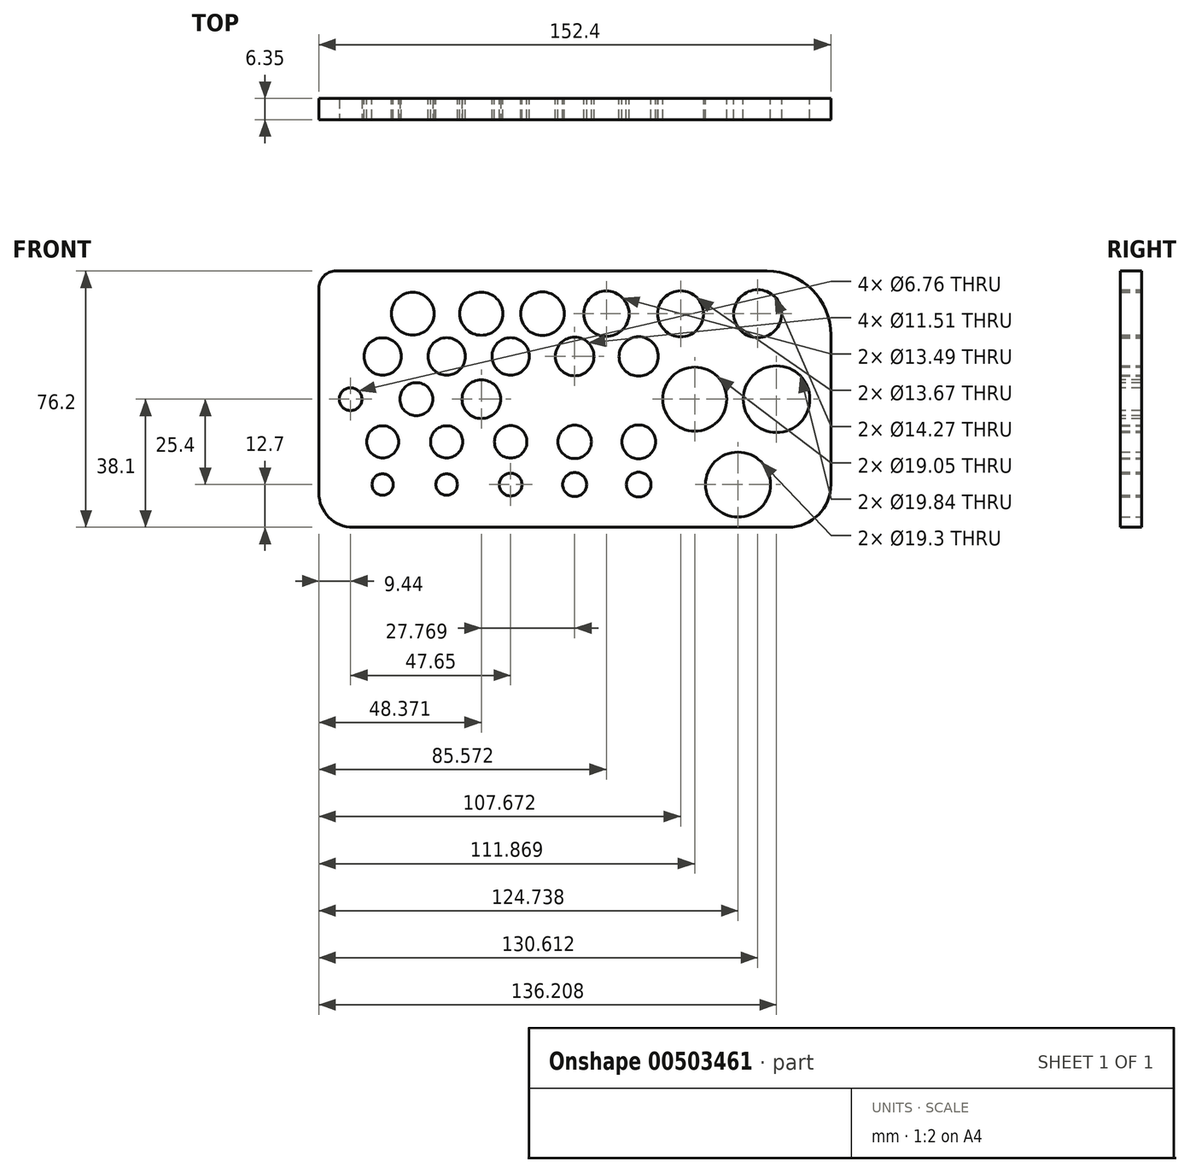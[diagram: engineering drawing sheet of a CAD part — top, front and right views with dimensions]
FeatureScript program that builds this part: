
annotation { "Feature Type Name" : "Feature", "Feature Type Description" : "" }
export const myFeature = defineFeature(function(context is Context, id is Id, definition is map)
    precondition{}
    {
        {
            var Q0;
            Q0=qCreatedBy(makeId("Front.planeOp"),FACE);
            var sketch = newSketch(context, id + "F0", { "sketchPlane" : qUnion([Q0])});
            skLineSegment(sketch, "E0.bottom", {"start": v(-76.2, 38.1) * mm, "end": v(76.2, 38.1) * mm});
            skLineSegment(sketch, "E0.top", {"start": v(-76.2, -38.1) * mm, "end": v(76.2, -38.1) * mm});
            skLineSegment(sketch, "E0.left", {"start": v(-76.2, 38.1) * mm, "end": v(-76.2, -38.1) * mm});
            skLineSegment(sketch, "E0.right", {"start": v(76.2, 38.1) * mm, "end": v(76.2, -38.1) * mm});
            skPoint(sketch, "E0.middle", {"position": v(0, 0) * mm});
            skLineSegment(sketch, "E1", {"start": v(-76.2, 0) * mm, "end": v(76.2, 0) * mm, "construction": true});
            skLineSegment(sketch, "E2", {"start": v(-76.2, 25.4) * mm, "end": v(76.2, 25.4) * mm, "construction": true});
            skLineSegment(sketch, "E3", {"start": v(76.2, -25.4) * mm, "end": v(-76.2, -25.4) * mm, "construction": true});
            skPoint(sketch, "E4", {"position": v(-57.2, -25.4) * mm});
            skCircle(sketch, "E5", {"center": v(-38.16, -25.4) * mm, "radius": 3.2 * mm});
            skCircle(sketch, "E6", {"center": v(-57.2, -25.4) * mm, "radius": 3.18 * mm});
            skCircle(sketch, "E7", {"center": v(-19.1, -25.4) * mm, "radius": 3.38 * mm});
            skCircle(sketch, "E8", {"center": v(-0.06, -25.4) * mm, "radius": 3.57 * mm});
            skCircle(sketch, "E9", {"center": v(19, -25.4) * mm, "radius": 3.68 * mm});
            skLineSegment(sketch, "E10", {"start": v(-76.2, 12.7) * mm, "end": v(76.2, 12.7) * mm, "construction": true});
            skLineSegment(sketch, "E11.MirrorCS", {"start": v(-76.2, -12.7) * mm, "end": v(76.2, -12.7) * mm, "construction": true});
            skPoint(sketch, "E12", {"position": v(-57.2, 12.7) * mm});
            skPoint(sketch, "E13", {"position": v(-57.2, 0) * mm});
            skPoint(sketch, "E14", {"position": v(-57.2, -12.7) * mm});
            skPoint(sketch, "E15", {"position": v(-38.16, 12.7) * mm});
            skPoint(sketch, "E16", {"position": v(-38.16, 0) * mm});
            skPoint(sketch, "E17", {"position": v(-38.16, -12.7) * mm});
            skPoint(sketch, "E18", {"position": v(-19.1, 12.7) * mm});
            skPoint(sketch, "E19", {"position": v(-19.1, 0) * mm});
            skPoint(sketch, "E20", {"position": v(-19.1, -12.7) * mm});
            skPoint(sketch, "E21", {"position": v(-0.06, 12.7) * mm});
            skPoint(sketch, "E22", {"position": v(-0.06, -12.7) * mm});
            skPoint(sketch, "E23", {"position": v(19, 12.7) * mm});
            skPoint(sketch, "E24", {"position": v(19, 0) * mm});
            skPoint(sketch, "E25", {"position": v(19, -12.7) * mm});
            skCircle(sketch, "E26", {"center": v(-57.2, -12.7) * mm, "radius": 4.76 * mm});
            skCircle(sketch, "E27", {"center": v(-38.16, -12.7) * mm, "radius": 4.79 * mm});
            skCircle(sketch, "E28", {"center": v(-19.1, -12.7) * mm, "radius": 4.83 * mm});
            skCircle(sketch, "E29", {"center": v(-0.06, -12.7) * mm, "radius": 4.97 * mm});
            skCircle(sketch, "E30", {"center": v(19, -12.7) * mm, "radius": 5.04 * mm});
            skCircle(sketch, "E31", {"center": v(-57.2, 12.7) * mm, "radius": 5.56 * mm});
            skCircle(sketch, "E32", {"center": v(-38.16, 12.7) * mm, "radius": 5.56 * mm});
            skCircle(sketch, "E33", {"center": v(-19.1, 12.7) * mm, "radius": 5.57 * mm});
            skCircle(sketch, "E34", {"center": v(-0.06, 12.7) * mm, "radius": 5.75 * mm});
            skCircle(sketch, "E35", {"center": v(19, 12.7) * mm, "radius": 5.84 * mm});
            skPoint(sketch, "E36", {"position": v(-48.26, 25.4) * mm});
            skPoint(sketch, "E37", {"position": v(-27.84, 25.4) * mm});
            skPoint(sketch, "E38", {"position": v(-9.65, 25.4) * mm});
            skPoint(sketch, "E39", {"position": v(9.37, 25.4) * mm});
            skCircle(sketch, "E40", {"center": v(-48.26, 25.4) * mm, "radius": 6.35 * mm});
            skCircle(sketch, "E41", {"center": v(-27.84, 25.4) * mm, "radius": 6.41 * mm});
            skCircle(sketch, "E42", {"center": v(-9.65, 25.4) * mm, "radius": 6.48 * mm});
            skCircle(sketch, "E43", {"center": v(9.37, 25.4) * mm, "radius": 6.74 * mm});
            skPoint(sketch, "E44", {"position": v(31.47, 25.4) * mm});
            skCircle(sketch, "E45", {"center": v(31.47, 25.4) * mm, "radius": 6.83 * mm});
            skPoint(sketch, "E46", {"position": v(54.41, 25.4) * mm});
            skCircle(sketch, "E47", {"center": v(54.41, 25.4) * mm, "radius": 7.14 * mm});
            skPoint(sketch, "E48", {"position": v(34.55, -12.7) * mm});
            skCircle(sketch, "E49", {"center": v(35.67, 0) * mm, "radius": 9.53 * mm});
            skCircle(sketch, "E50", {"center": v(60, 0) * mm, "radius": 9.92 * mm});
            skCircle(sketch, "E51", {"center": v(48.54, -25.4) * mm, "radius": 9.65 * mm});
            skSolve(sketch);
        }
        {
            var Q0;
            Q0=makeQuery(id+"F0.imprint","IMPRINT",FACE,{"disambiguationData":[TD([[makeQuery(id+"F0.imprint","IMPRINT",EDGE,{"derivedFrom":sQuery(id+"F0.wireOp",EDGE,"E0.bottom")}),-1.0]])]});
            extrude(context, id + "F1", {"entities" : qUnion([Q0]), "depth" : 6.35 * mm, "offsetDistance" : 25.4 * mm});
        }
        {
            var Q0;
            Q0=makeQuery(id+"F1.opExtrude","SWEPT_EDGE",EDGE,{"disambiguationData":[OSD([sQuery(id+"F0.wireOp",EDGE,"E0.bottom"),sQuery(id+"F0.wireOp",EDGE,"E0.left")])]});
            fillet(context, id + "F2", {"entities" : qUnion([Q0]), "radius" : 5.08 * mm, "tangentPropagation" : true, "allowEdgeOverflow" : false});
        }
        {
            var Q0;
            Q0=makeQuery(id+"F1.opExtrude","SWEPT_EDGE",EDGE,{"disambiguationData":[OSD([sQuery(id+"F0.wireOp",EDGE,"E0.top"),sQuery(id+"F0.wireOp",EDGE,"E0.left")])]});
            fillet(context, id + "F3", {"entities" : qUnion([Q0]), "radius" : 10.16 * mm, "tangentPropagation" : true, "allowEdgeOverflow" : false});
        }
        {
            var Q0;
            Q0=makeQuery(id+"F1.opExtrude","SWEPT_EDGE",EDGE,{"disambiguationData":[OSD([sQuery(id+"F0.wireOp",EDGE,"E0.top"),sQuery(id+"F0.wireOp",EDGE,"E0.right")])]});
            fillet(context, id + "F4", {"entities" : qUnion([Q0]), "radius" : 12.7 * mm, "tangentPropagation" : true, "allowEdgeOverflow" : false});
        }
        {
            var Q0;
            Q0=makeQuery(id+"F1.opExtrude","SWEPT_EDGE",EDGE,{"disambiguationData":[OSD([sQuery(id+"F0.wireOp",EDGE,"E0.bottom"),sQuery(id+"F0.wireOp",EDGE,"E0.right")])]});
            fillet(context, id + "F5", {"entities" : qUnion([Q0]), "radius" : 19.05 * mm, "tangentPropagation" : true, "allowEdgeOverflow" : false});
        }
        {
            var Q0;
            Q0=makeQuery(id+"F1.opExtrude","CAP_FACE",FACE,{"disambiguationData":[OSD([sQuery(id+"F0.wireOp",EDGE,"E0.bottom"),sQuery(id+"F0.wireOp",EDGE,"E0.top"),sQuery(id+"F0.wireOp",EDGE,"E0.left"),sQuery(id+"F0.wireOp",EDGE,"E0.right"),sQuery(id+"F0.wireOp",EDGE,"E5"),sQuery(id+"F0.wireOp",EDGE,"E6"),sQuery(id+"F0.wireOp",EDGE,"E7"),sQuery(id+"F0.wireOp",EDGE,"E8"),sQuery(id+"F0.wireOp",EDGE,"E9"),sQuery(id+"F0.wireOp",EDGE,"E26"),sQuery(id+"F0.wireOp",EDGE,"E27"),sQuery(id+"F0.wireOp",EDGE,"E28"),sQuery(id+"F0.wireOp",EDGE,"E29"),sQuery(id+"F0.wireOp",EDGE,"E30"),sQuery(id+"F0.wireOp",EDGE,"E31"),sQuery(id+"F0.wireOp",EDGE,"E32"),sQuery(id+"F0.wireOp",EDGE,"E33"),sQuery(id+"F0.wireOp",EDGE,"E34"),sQuery(id+"F0.wireOp",EDGE,"E35"),sQuery(id+"F0.wireOp",EDGE,"E40"),sQuery(id+"F0.wireOp",EDGE,"E41"),sQuery(id+"F0.wireOp",EDGE,"E42"),sQuery(id+"F0.wireOp",EDGE,"E43"),sQuery(id+"F0.wireOp",EDGE,"E45"),sQuery(id+"F0.wireOp",EDGE,"E47"),sQuery(id+"F0.wireOp",EDGE,"E49"),sQuery(id+"F0.wireOp",EDGE,"E50"),sQuery(id+"F0.wireOp",EDGE,"E51")])],"isStart":false});
            var sketch = newSketch(context, id + "F6", { "sketchPlane" : qUnion([Q0])});
            skPoint(sketch, "E52", {"position": v(-66.76, 0) * mm});
            skPoint(sketch, "E53", {"position": v(-49.16, 0) * mm});
            skPoint(sketch, "E54", {"position": v(-27.34, 0) * mm});
            skSolve(sketch);
        }
        {
            var Q0;
            Q0=sQuery(id+"F6.wireOp",VERTEX,"E52");
            var Q1;
            Q1=makeQuery(id+"F1.opExtrude","SWEPT_BODY",BODY,{"disambiguationData":[OSD([sQuery(id+"F0.wireOp",EDGE,"E0.bottom"),sQuery(id+"F0.wireOp",EDGE,"E0.top"),sQuery(id+"F0.wireOp",EDGE,"E0.left"),sQuery(id+"F0.wireOp",EDGE,"E0.right"),sQuery(id+"F0.wireOp",EDGE,"E5"),sQuery(id+"F0.wireOp",EDGE,"E6"),sQuery(id+"F0.wireOp",EDGE,"E7"),sQuery(id+"F0.wireOp",EDGE,"E8"),sQuery(id+"F0.wireOp",EDGE,"E9"),sQuery(id+"F0.wireOp",EDGE,"E26"),sQuery(id+"F0.wireOp",EDGE,"E27"),sQuery(id+"F0.wireOp",EDGE,"E28"),sQuery(id+"F0.wireOp",EDGE,"E29"),sQuery(id+"F0.wireOp",EDGE,"E30"),sQuery(id+"F0.wireOp",EDGE,"E31"),sQuery(id+"F0.wireOp",EDGE,"E32"),sQuery(id+"F0.wireOp",EDGE,"E33"),sQuery(id+"F0.wireOp",EDGE,"E34"),sQuery(id+"F0.wireOp",EDGE,"E35"),sQuery(id+"F0.wireOp",EDGE,"E40"),sQuery(id+"F0.wireOp",EDGE,"E41"),sQuery(id+"F0.wireOp",EDGE,"E42"),sQuery(id+"F0.wireOp",EDGE,"E43"),sQuery(id+"F0.wireOp",EDGE,"E45"),sQuery(id+"F0.wireOp",EDGE,"E47"),sQuery(id+"F0.wireOp",EDGE,"E49"),sQuery(id+"F0.wireOp",EDGE,"E50"),sQuery(id+"F0.wireOp",EDGE,"E51")])]});
            hole(context, id + "F7", {"style" : HoleStyle.SIMPLE, "endStyle" : HoleEndStyle.THROUGH, "standardTappedOrClearance" : lookupTablePath({ "fit" : "Normal (ASME)", "standard" : "ANSI", "size" : "1/4", "type" : "Clearance" }), "standardBlindInLast" : lookupTablePath({ "fit" : "Free", "standard" : "ANSI", "size" : "1/4", "type" : "Clearance" }), "holeDiameter" : 6.76 * mm, "majorDiameter" : 6.35 * mm, "isTappedThrough" : true, "tappedDepth" : 12.7 * mm, "tapClearance" : 3, "locations" : qUnion([Q0]), "scope" : qUnion([Q1])});
        }
        {
            var Q0;
            Q0=makeQuery(id+"F1.opExtrude","CAP_FACE",FACE,{"disambiguationData":[OSD([sQuery(id+"F0.wireOp",EDGE,"E0.bottom"),sQuery(id+"F0.wireOp",EDGE,"E0.top"),sQuery(id+"F0.wireOp",EDGE,"E0.left"),sQuery(id+"F0.wireOp",EDGE,"E0.right"),sQuery(id+"F0.wireOp",EDGE,"E5"),sQuery(id+"F0.wireOp",EDGE,"E6"),sQuery(id+"F0.wireOp",EDGE,"E7"),sQuery(id+"F0.wireOp",EDGE,"E8"),sQuery(id+"F0.wireOp",EDGE,"E9"),sQuery(id+"F0.wireOp",EDGE,"E26"),sQuery(id+"F0.wireOp",EDGE,"E27"),sQuery(id+"F0.wireOp",EDGE,"E28"),sQuery(id+"F0.wireOp",EDGE,"E29"),sQuery(id+"F0.wireOp",EDGE,"E30"),sQuery(id+"F0.wireOp",EDGE,"E31"),sQuery(id+"F0.wireOp",EDGE,"E32"),sQuery(id+"F0.wireOp",EDGE,"E33"),sQuery(id+"F0.wireOp",EDGE,"E34"),sQuery(id+"F0.wireOp",EDGE,"E35"),sQuery(id+"F0.wireOp",EDGE,"E40"),sQuery(id+"F0.wireOp",EDGE,"E41"),sQuery(id+"F0.wireOp",EDGE,"E42"),sQuery(id+"F0.wireOp",EDGE,"E43"),sQuery(id+"F0.wireOp",EDGE,"E45"),sQuery(id+"F0.wireOp",EDGE,"E47"),sQuery(id+"F0.wireOp",EDGE,"E49"),sQuery(id+"F0.wireOp",EDGE,"E50"),sQuery(id+"F0.wireOp",EDGE,"E51")])],"isStart":false});
            var sketch = newSketch(context, id + "F8", { "sketchPlane" : qUnion([Q0])});
            skPoint(sketch, "E55", {"position": v(-47.17, 0) * mm});
            skSolve(sketch);
        }
        {
            var Q0;
            Q0=sQuery(id+"F8.wireOp",VERTEX,"E55");
            var Q1;
            Q1=makeQuery(id+"F1.opExtrude","SWEPT_BODY",BODY,{"disambiguationData":[OSD([sQuery(id+"F0.wireOp",EDGE,"E0.bottom"),sQuery(id+"F0.wireOp",EDGE,"E0.top"),sQuery(id+"F0.wireOp",EDGE,"E0.left"),sQuery(id+"F0.wireOp",EDGE,"E0.right"),sQuery(id+"F0.wireOp",EDGE,"E5"),sQuery(id+"F0.wireOp",EDGE,"E6"),sQuery(id+"F0.wireOp",EDGE,"E7"),sQuery(id+"F0.wireOp",EDGE,"E8"),sQuery(id+"F0.wireOp",EDGE,"E9"),sQuery(id+"F0.wireOp",EDGE,"E26"),sQuery(id+"F0.wireOp",EDGE,"E27"),sQuery(id+"F0.wireOp",EDGE,"E28"),sQuery(id+"F0.wireOp",EDGE,"E29"),sQuery(id+"F0.wireOp",EDGE,"E30"),sQuery(id+"F0.wireOp",EDGE,"E31"),sQuery(id+"F0.wireOp",EDGE,"E32"),sQuery(id+"F0.wireOp",EDGE,"E33"),sQuery(id+"F0.wireOp",EDGE,"E34"),sQuery(id+"F0.wireOp",EDGE,"E35"),sQuery(id+"F0.wireOp",EDGE,"E40"),sQuery(id+"F0.wireOp",EDGE,"E41"),sQuery(id+"F0.wireOp",EDGE,"E42"),sQuery(id+"F0.wireOp",EDGE,"E43"),sQuery(id+"F0.wireOp",EDGE,"E45"),sQuery(id+"F0.wireOp",EDGE,"E47"),sQuery(id+"F0.wireOp",EDGE,"E49"),sQuery(id+"F0.wireOp",EDGE,"E50"),sQuery(id+"F0.wireOp",EDGE,"E51")])]});
            hole(context, id + "F9", {"style" : HoleStyle.SIMPLE, "endStyle" : HoleEndStyle.THROUGH, "standardTappedOrClearance" : lookupTablePath({ "fit" : "Close", "standard" : "ANSI", "size" : "3/8", "type" : "Clearance" }), "standardBlindInLast" : lookupTablePath({ "fit" : "Close", "standard" : "ANSI", "size" : "3/8", "type" : "Clearance" }), "holeDiameter" : 9.8 * mm, "majorDiameter" : 6.35 * mm, "isTappedThrough" : true, "tappedDepth" : 12.7 * mm, "tapClearance" : 3, "locations" : qUnion([Q0]), "scope" : qUnion([Q1])});
        }
        {
            var Q0;
            Q0=makeQuery(id+"F1.opExtrude","CAP_FACE",FACE,{"disambiguationData":[OSD([sQuery(id+"F0.wireOp",EDGE,"E0.bottom"),sQuery(id+"F0.wireOp",EDGE,"E0.top"),sQuery(id+"F0.wireOp",EDGE,"E0.left"),sQuery(id+"F0.wireOp",EDGE,"E0.right"),sQuery(id+"F0.wireOp",EDGE,"E5"),sQuery(id+"F0.wireOp",EDGE,"E6"),sQuery(id+"F0.wireOp",EDGE,"E7"),sQuery(id+"F0.wireOp",EDGE,"E8"),sQuery(id+"F0.wireOp",EDGE,"E9"),sQuery(id+"F0.wireOp",EDGE,"E26"),sQuery(id+"F0.wireOp",EDGE,"E27"),sQuery(id+"F0.wireOp",EDGE,"E28"),sQuery(id+"F0.wireOp",EDGE,"E29"),sQuery(id+"F0.wireOp",EDGE,"E30"),sQuery(id+"F0.wireOp",EDGE,"E31"),sQuery(id+"F0.wireOp",EDGE,"E32"),sQuery(id+"F0.wireOp",EDGE,"E33"),sQuery(id+"F0.wireOp",EDGE,"E34"),sQuery(id+"F0.wireOp",EDGE,"E35"),sQuery(id+"F0.wireOp",EDGE,"E40"),sQuery(id+"F0.wireOp",EDGE,"E41"),sQuery(id+"F0.wireOp",EDGE,"E42"),sQuery(id+"F0.wireOp",EDGE,"E43"),sQuery(id+"F0.wireOp",EDGE,"E45"),sQuery(id+"F0.wireOp",EDGE,"E47"),sQuery(id+"F0.wireOp",EDGE,"E49"),sQuery(id+"F0.wireOp",EDGE,"E50"),sQuery(id+"F0.wireOp",EDGE,"E51")])],"isStart":false});
            var sketch = newSketch(context, id + "F10", { "sketchPlane" : qUnion([Q0])});
            skPoint(sketch, "E56", {"position": v(-27.83, 0) * mm});
            skSolve(sketch);
        }
        {
            var Q0;
            Q0=sQuery(id+"F10.wireOp",VERTEX,"E56");
            var Q1;
            Q1=makeQuery(id+"F1.opExtrude","SWEPT_BODY",BODY,{"disambiguationData":[OSD([sQuery(id+"F0.wireOp",EDGE,"E0.bottom"),sQuery(id+"F0.wireOp",EDGE,"E0.top"),sQuery(id+"F0.wireOp",EDGE,"E0.left"),sQuery(id+"F0.wireOp",EDGE,"E0.right"),sQuery(id+"F0.wireOp",EDGE,"E5"),sQuery(id+"F0.wireOp",EDGE,"E6"),sQuery(id+"F0.wireOp",EDGE,"E7"),sQuery(id+"F0.wireOp",EDGE,"E8"),sQuery(id+"F0.wireOp",EDGE,"E9"),sQuery(id+"F0.wireOp",EDGE,"E26"),sQuery(id+"F0.wireOp",EDGE,"E27"),sQuery(id+"F0.wireOp",EDGE,"E28"),sQuery(id+"F0.wireOp",EDGE,"E29"),sQuery(id+"F0.wireOp",EDGE,"E30"),sQuery(id+"F0.wireOp",EDGE,"E31"),sQuery(id+"F0.wireOp",EDGE,"E32"),sQuery(id+"F0.wireOp",EDGE,"E33"),sQuery(id+"F0.wireOp",EDGE,"E34"),sQuery(id+"F0.wireOp",EDGE,"E35"),sQuery(id+"F0.wireOp",EDGE,"E40"),sQuery(id+"F0.wireOp",EDGE,"E41"),sQuery(id+"F0.wireOp",EDGE,"E42"),sQuery(id+"F0.wireOp",EDGE,"E43"),sQuery(id+"F0.wireOp",EDGE,"E45"),sQuery(id+"F0.wireOp",EDGE,"E47"),sQuery(id+"F0.wireOp",EDGE,"E49"),sQuery(id+"F0.wireOp",EDGE,"E50"),sQuery(id+"F0.wireOp",EDGE,"E51")])]});
            hole(context, id + "F11", {"style" : HoleStyle.SIMPLE, "endStyle" : HoleEndStyle.THROUGH, "standardTappedOrClearance" : lookupTablePath({ "fit" : "Close", "standard" : "ANSI", "size" : "7/16", "type" : "Clearance" }), "standardBlindInLast" : lookupTablePath({ "fit" : "Close", "standard" : "ANSI", "size" : "7/16", "type" : "Clearance" }), "holeDiameter" : 11.5 * mm, "majorDiameter" : 6.35 * mm, "isTappedThrough" : true, "tappedDepth" : 12.7 * mm, "tapClearance" : 3, "locations" : qUnion([Q0]), "scope" : qUnion([Q1])});
        }
    });
